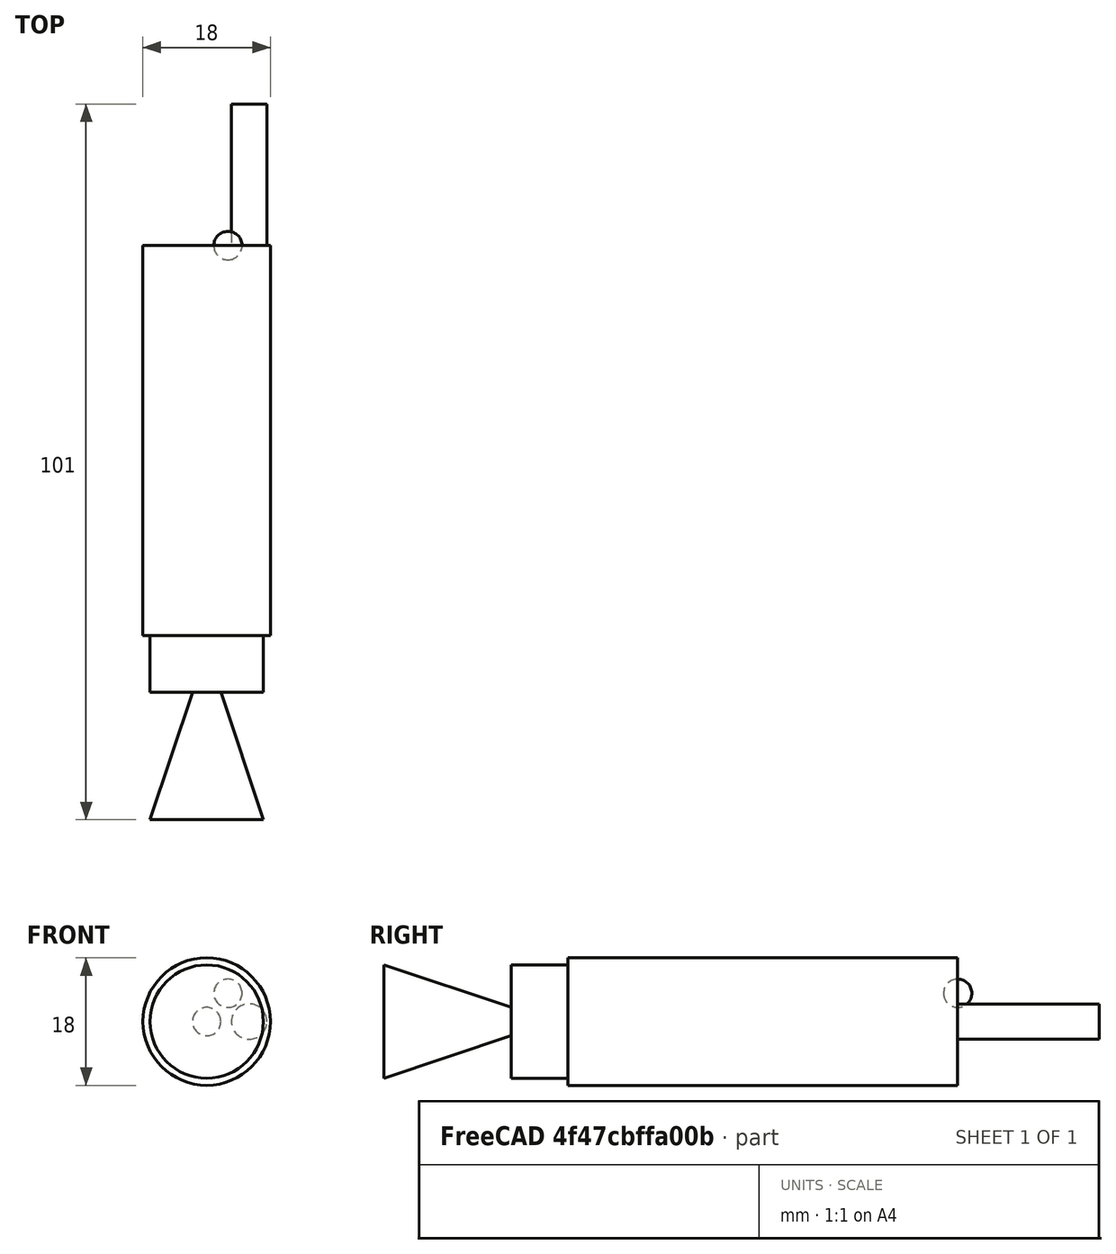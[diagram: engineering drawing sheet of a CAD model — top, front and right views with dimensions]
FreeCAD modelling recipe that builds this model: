
FCSTD DOCUMENT  (FreeCAD 0.16R4706 (Git))
Label: Sonda-Capacitiva
License: All rights reserved
LicenseURL: http://en.wikipedia.org/wiki/All_rights_reserved
objects: Part::Cylinder×3, Part::Cone×1, Part::Sphere×1, Part::Compound×1
note: 6 computed .brp shape members not serialized (recipe doc carries the construction recipe); baked Part::Feature solids carry a one-line shape summary decoded from their .brp

FEATURE [Part::Cylinder] Cylinder
  Angle = 360
  Height = 55
  Placement = pos=(12,6,6) rot=(1,0,0;1.5708rad)
  Radius = 9
FEATURE [Part::Cylinder] Cylinder001
  Angle = 360
  Height = 8
  Placement = pos=(12,-49,6) rot=(1,0,0;1.5708rad)
  Radius = 8
FEATURE [Part::Cone] Cone
  Angle = 360
  Height = 18
  Placement = pos=(12,-57,6) rot=(1,0,0;1.5708rad)
  Radius1 = 2
  Radius2 = 8
FEATURE [Part::Cylinder] Cylinder002
  Angle = 360
  Height = 20
  Placement = pos=(18,26,6) rot=(1,0,0;1.5708rad)
  Radius = 2.5
FEATURE [Part::Sphere] Sphere
  Angle1 = -90
  Angle2 = 90
  Angle3 = 360
  Placement = pos=(15,6,10) rot=(1,0,0;1.5708rad)
  Radius = 2
FEATURE [Part::Compound] Compound  label="SondaCapacitiva"
  Links = -> [Cylinder002,Cylinder,Sphere,Cylinder001,Cone]
